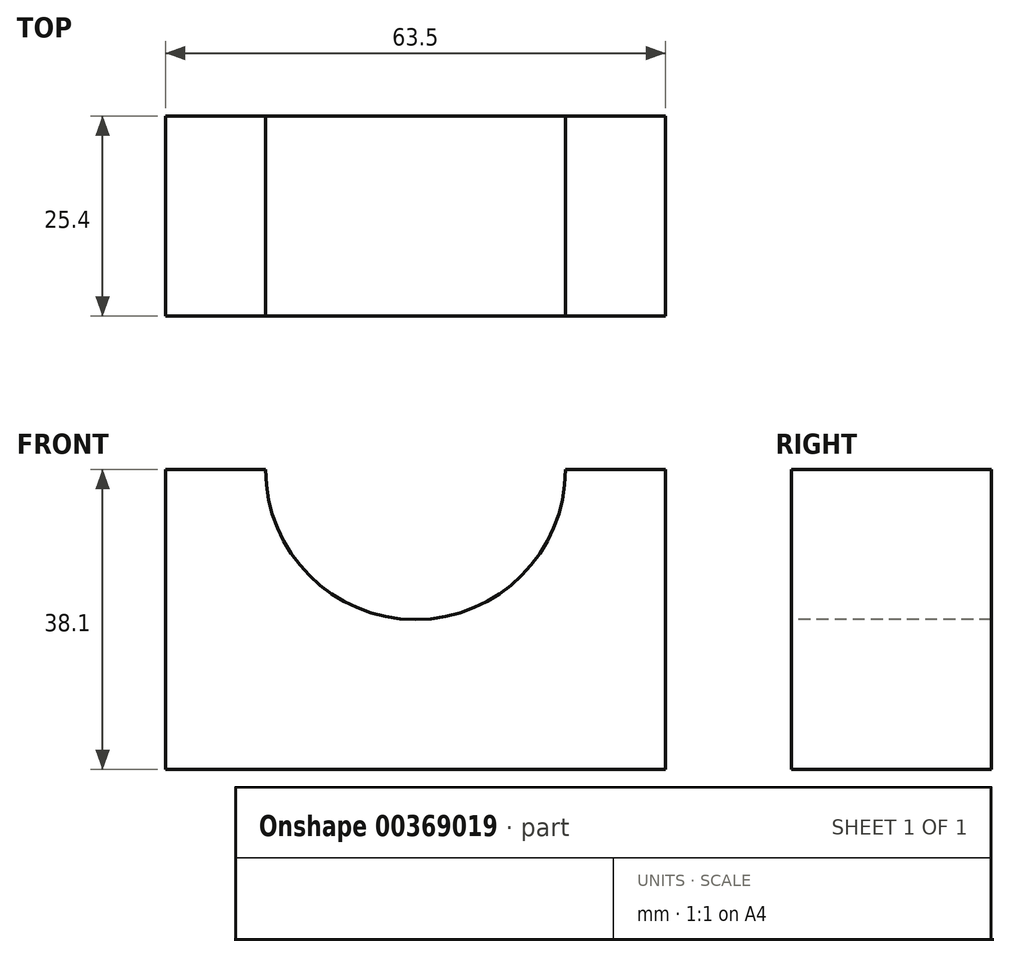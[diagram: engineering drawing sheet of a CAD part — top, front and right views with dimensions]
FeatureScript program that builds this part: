
annotation { "Feature Type Name" : "Feature", "Feature Type Description" : "" }
export const myFeature = defineFeature(function(context is Context, id is Id, definition is map)
    precondition{}
    {
        {
            var Q0;
            Q0=qCreatedBy(makeId("Front.planeOp"),FACE);
            var sketch = newSketch(context, id + "F0", { "sketchPlane" : qUnion([Q0])});
            skLineSegment(sketch, "E0", {"start": v(-29.82, 0) * mm, "end": v(-29.82, 38.1) * mm});
            skLineSegment(sketch, "E1", {"start": v(-29.82, 38.1) * mm, "end": v(33.68, 38.1) * mm});
            skLineSegment(sketch, "E2", {"start": v(33.68, 38.1) * mm, "end": v(33.68, 0) * mm});
            skLineSegment(sketch, "E3", {"start": v(33.68, 0) * mm, "end": v(-29.82, 0) * mm});
            skSolve(sketch);
        }
        {
            var Q0;
            Q0=makeQuery(id+"F0.imprint","IMPRINT",FACE,{"disambiguationData":[TD([[makeQuery(id+"F0.imprint","IMPRINT",EDGE,{"derivedFrom":sQuery(id+"F0.wireOp",EDGE,"E0")}),-1.0]])]});
            extrude(context, id + "F1", {"entities" : qUnion([Q0]), "depth" : 25.4 * mm});
        }
        {
            var Q0;
            Q0=makeQuery(id+"F1.opExtrude","CAP_FACE",FACE,{"disambiguationData":[OSD([sQuery(id+"F0.wireOp",EDGE,"E0"),sQuery(id+"F0.wireOp",EDGE,"E1"),sQuery(id+"F0.wireOp",EDGE,"E2"),sQuery(id+"F0.wireOp",EDGE,"E3")])],"isStart":false});
            var sketch = newSketch(context, id + "F2", { "sketchPlane" : qUnion([Q0])});
            skPoint(sketch, "E4", {"position": v(-17.12, 38.1) * mm});
            skPoint(sketch, "E5", {"position": v(20.98, 38.1) * mm});
            skArc(sketch, "E6", {"start": v(-17.12, 38.1) * mm, "mid": v(1.93, 19.05) * mm, "end": v(20.98, 38.1) * mm});
            skSolve(sketch);
        }
        {
            var Q0;
            {var subQ0=sQuery(id+"F2.wireOp",EDGE,"E6");Q0=makeQuery(id+"F2.imprint","IMPRINT",FACE,{"disambiguationData":[TD([[makeQuery(id+"F2.imprint","IMPRINT",EDGE,{"derivedFrom":subQ0}),1.0]])]});}
            extrude(context, id + "F3", {"entities" : qUnion([Q0]), "operationType" : NewBodyOperationType.REMOVE, "oppositeDirection" : true, "depth" : 25.4 * mm});
        }
    });
